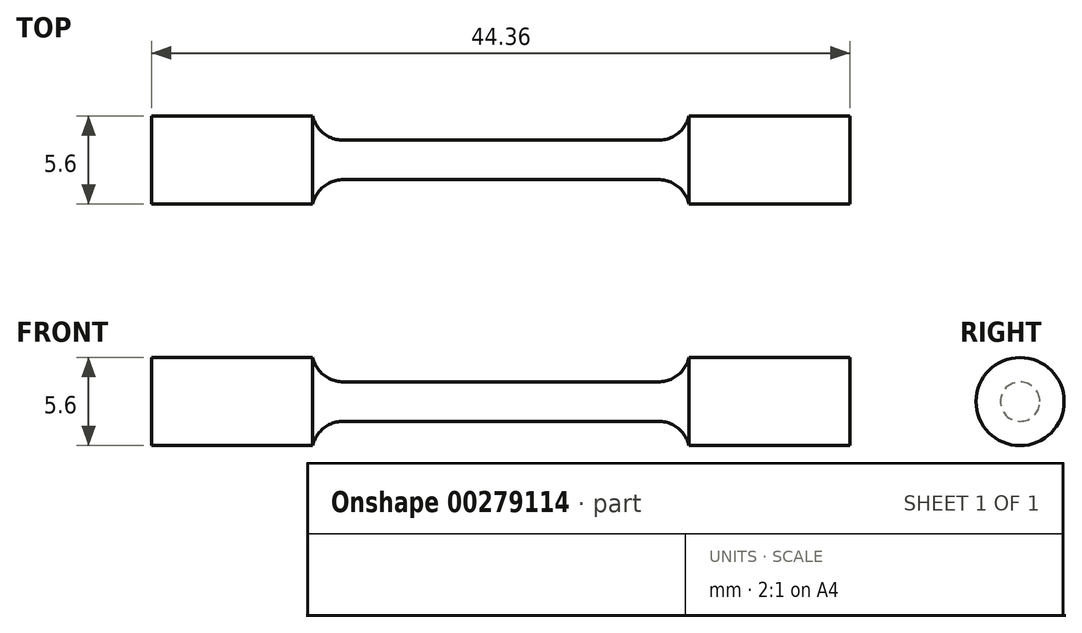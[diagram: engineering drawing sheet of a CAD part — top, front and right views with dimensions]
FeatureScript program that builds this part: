
annotation { "Feature Type Name" : "Feature", "Feature Type Description" : "" }
export const myFeature = defineFeature(function(context is Context, id is Id, definition is map)
    precondition{}
    {
        {
            var Q0;
            Q0=qCreatedBy(makeId("Front.planeOp"),FACE);
            var sketch = newSketch(context, id + "F0", { "sketchPlane" : qUnion([Q0])});
            skLineSegment(sketch, "E0", {"start": v(0, 1.25) * mm, "end": v(10, 1.25) * mm});
            skArc(sketch, "E1", {"start": v(10, 1.25) * mm, "mid": v(11.24, 1.68) * mm, "end": v(11.95, 2.8) * mm});
            skLineSegment(sketch, "E2", {"start": v(11.95, 2.8) * mm, "end": v(22.18, 2.8) * mm});
            skLineSegment(sketch, "E3", {"start": v(22.18, 2.8) * mm, "end": v(22.18, 0) * mm});
            skLineSegment(sketch, "E4.MirrorCS", {"start": v(-22.18, 2.8) * mm, "end": v(-22.18, 0) * mm});
            skArc(sketch, "E5.MirrorCS", {"start": v(-10, 1.25) * mm, "mid": v(-11.24, 1.68) * mm, "end": v(-11.95, 2.8) * mm});
            skLineSegment(sketch, "E6.MirrorCS", {"start": v(0, 1.25) * mm, "end": v(-10, 1.25) * mm});
            skLineSegment(sketch, "E7.MirrorCS", {"start": v(-11.95, 2.8) * mm, "end": v(-22.18, 2.8) * mm});
            skLineSegment(sketch, "E8", {"start": v(-22.18, 0) * mm, "end": v(22.18, 0) * mm});
            skSolve(sketch);
        }
        {
            var Q0;
            Q0 = qSketchRegion(id + "F0", true);
            var Q1;
            Q1=sQuery(id+"F0.wireOp",EDGE,"E8");
            revolve(context, id + "F1", {"entities" : qUnion([Q0]), "axis" : qUnion([Q1]), "revolveType" : RevolveType.FULL});
        }
    });
